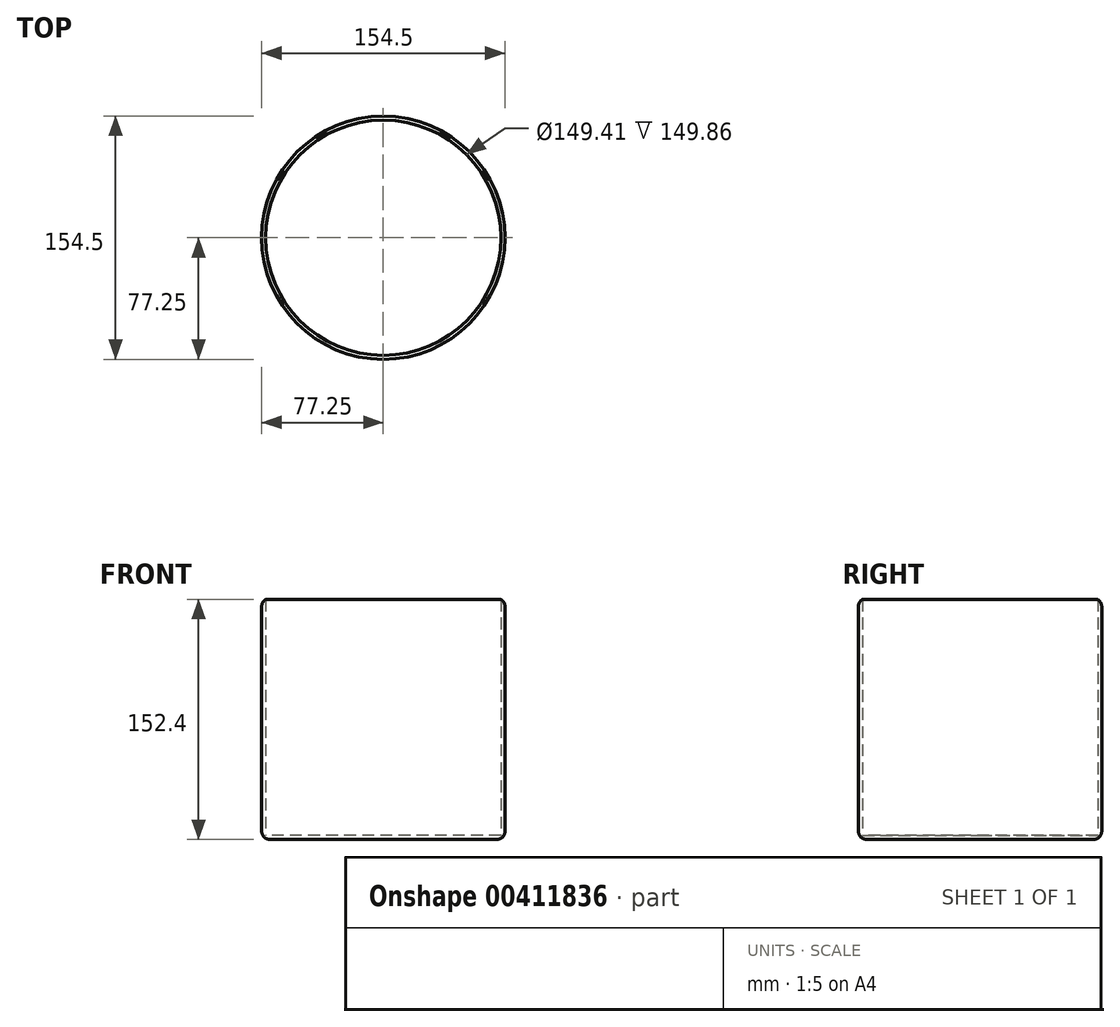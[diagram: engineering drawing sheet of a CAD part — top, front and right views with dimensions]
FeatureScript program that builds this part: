
annotation { "Feature Type Name" : "Feature", "Feature Type Description" : "" }
export const myFeature = defineFeature(function(context is Context, id is Id, definition is map)
    precondition{}
    {
        {
            var Q0;
            Q0=qCreatedBy(makeId("Top.planeOp"),FACE);
            var sketch = newSketch(context, id + "F0", { "sketchPlane" : qUnion([Q0])});
            skCircle(sketch, "E0", {"center": v(0, 0) * mm, "radius": 77.25 * mm});
            skSolve(sketch);
        }
        {
            var Q0;
            Q0=makeQuery(id+"F0.imprint","IMPRINT",FACE,{"disambiguationData":[TD([[makeQuery(id+"F0.imprint","IMPRINT",EDGE,{"derivedFrom":sQuery(id+"F0.wireOp",EDGE,"E0")}),1.0]])]});
            extrude(context, id + "F1", {"entities" : qUnion([Q0]), "depth" : 152.4 * mm});
        }
        {
            var Q0;
            Q0=makeQuery(id+"F1.opExtrude","CAP_FACE",FACE,{"disambiguationData":[OSD([sQuery(id+"F0.wireOp",EDGE,"E0")])],"isStart":false});
            shell(context, id + "F2", {"entities" : qUnion([Q0]), "thickness" : 2.54 * mm});
        }
        {
            var Q0;
            Q0=makeQuery(id+"F1.opExtrude","SWEPT_FACE",FACE,{"disambiguationData":[OSD([sQuery(id+"F0.wireOp",EDGE,"E0")])]});
            fillet(context, id + "F3", {"entities" : qUnion([Q0]), "radius" : 5.08 * mm, "tangentPropagation" : true, "allowEdgeOverflow" : false});
        }
    });
